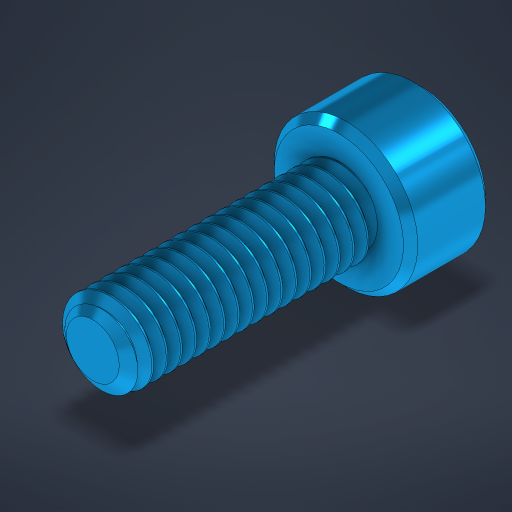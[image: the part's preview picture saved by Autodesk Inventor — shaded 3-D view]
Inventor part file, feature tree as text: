
AUTODESK INVENTOR PART (.ipt)
format: ipt  version: 2024 (Build 280153000, 153)  size: 742,400 bytes
history: native  units: in
note: dims shown in document units (in); Inventor stores cm internally (conversion verified against a paired STEP export)
features: chamfer x1
ambient origin geometry x8: Origin, YZ Plane, XZ Plane, XY Plane, X Axis, Y Axis, Z Axis, Center Point
bodies: Solid1 (feature_tree)
feature tree (1):
  chamfer  "Chamfer1"  [1 undecoded]
note: 1 required parameter value undecoded (feature->parameter linkage not recoverable at this tier; creation-order binding heuristic only, values carry confidence <= 0.55)
